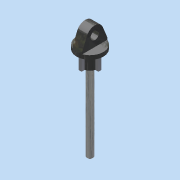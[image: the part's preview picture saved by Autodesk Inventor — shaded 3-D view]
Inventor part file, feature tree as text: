
AUTODESK INVENTOR PART (.ipt)
format: ipt  version: 2011 SP1 (Build 150282100, 282)  size: 143,872 bytes
history: native  units: in
note: dims shown in document units (in); Inventor stores cm internally (conversion verified against a paired STEP export)
features: extrude x6, sketch x6, chamfer x1, plane x1
ambient origin geometry x8: Origin, YZ Plane, XZ Plane, XY Plane, X Axis, Y Axis, Z Axis, Center Point
bodies: Solid1 (feature_tree)
feature tree (14):
  extrude  "Extrusion1"  Depth=2.0in TaperAngle=0.0deg
  chamfer  "Chamfer1"  Distance=0.0312in Angle=45.0deg
  extrude  "Extrusion2"  Depth=0.35in TaperAngle=0.0deg
  extrude  "Extrusion3"  Depth=0.1in TaperAngle=0.0deg
  extrude  "Extrusion4"  Depth=0.43in
  extrude  "Extrusion5"  Depth=0.24in TaperAngle=0.0deg
  extrude  "Extrusion6"  Depth=0.5in
  plane  "Work Plane1"
  sketch  "Sketch2"  dims[d0=0.156in d1=2.0in d2=0.0in d3=0.0312in d4=0.125in d5=45.0deg]
  sketch  "Sketch3"  dims[d6=0.35in d7=0.35in d8=0.0in]
  sketch  "Sketch4"  dims[d9=0.67in d10=0.1in d11=0.0in]
  sketch  "Sketch5"  dims[d12=0.21in d13=0.43in]
  sketch  "Sketch6"  dims[d14=0.47in d15=0.24in d16=0.0in]
  sketch  "Sketch7"  dims[d17=0.5in d18=0.0in d19=0.5in d20=0.08in d21=0.04in d22=1.5748in d24=360.0deg d26=0.35in d27=0.0in]
